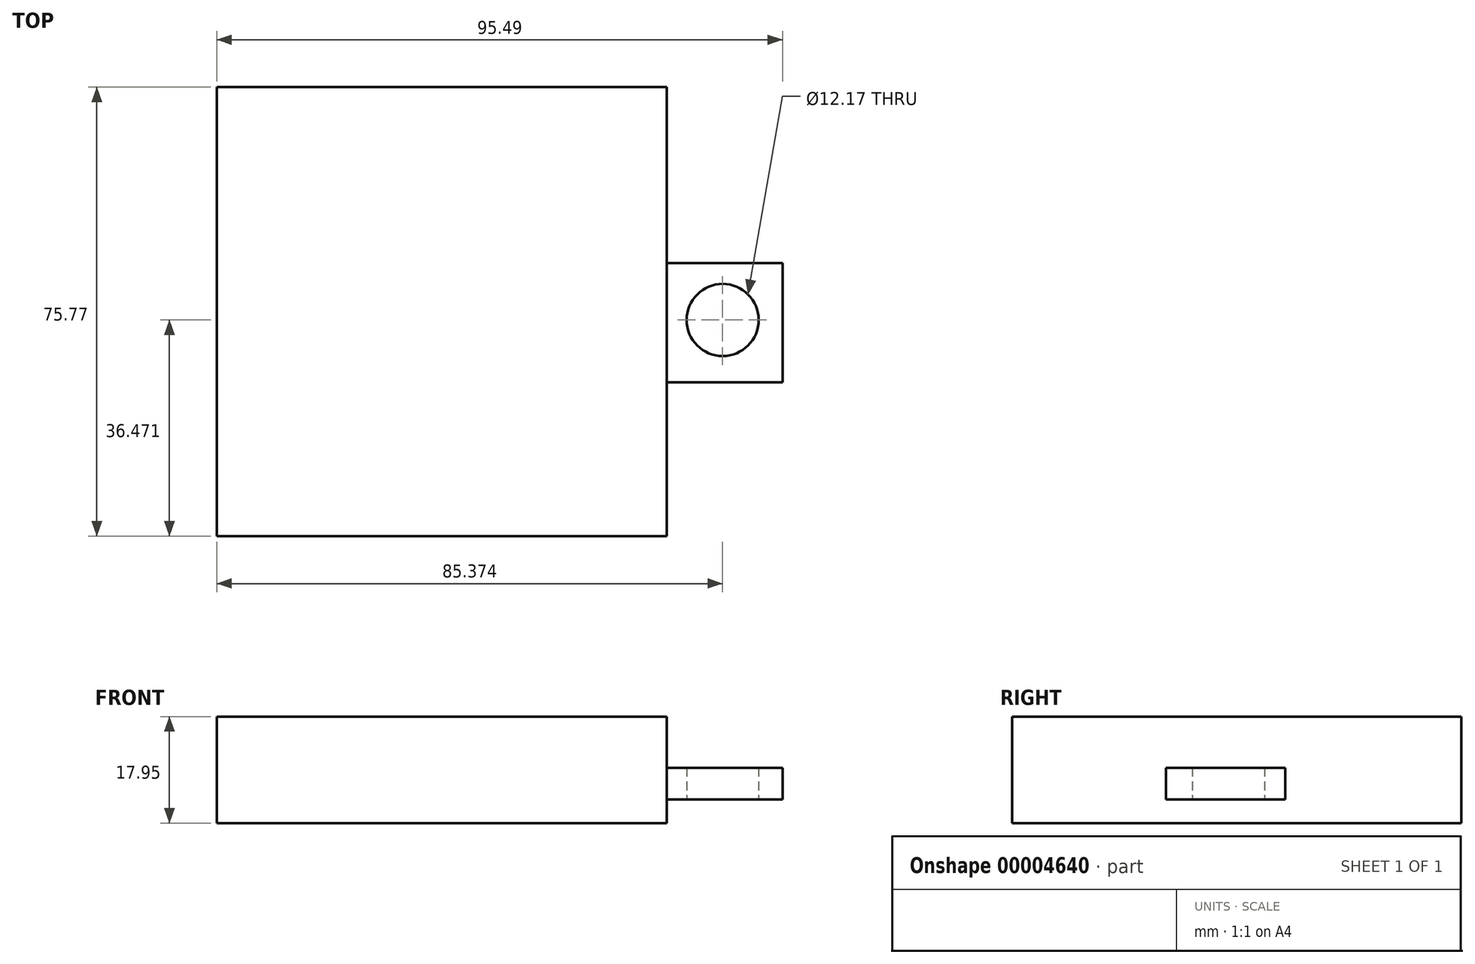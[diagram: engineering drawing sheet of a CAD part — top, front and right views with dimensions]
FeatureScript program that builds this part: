
annotation { "Feature Type Name" : "Feature", "Feature Type Description" : "" }
export const myFeature = defineFeature(function(context is Context, id is Id, definition is map)
    precondition{}
    {
        {
            var Q0;
            Q0=qCreatedBy(makeId("Top.planeOp"),FACE);
            var sketch = newSketch(context, id + "F0", { "sketchPlane" : qUnion([Q0])});
            skLineSegment(sketch, "E0.bottom", {"start": v(0, 75.77) * mm, "end": v(-75.95, 75.77) * mm});
            skLineSegment(sketch, "E0.top", {"start": v(0, 0) * mm, "end": v(-75.95, 0) * mm});
            skLineSegment(sketch, "E0.left", {"start": v(0, 75.77) * mm, "end": v(0, 0) * mm});
            skLineSegment(sketch, "E0.right", {"start": v(-75.95, 75.77) * mm, "end": v(-75.95, 0) * mm});
            skLineSegment(sketch, "E1", {"start": v(-37.98, 75.77) * mm, "end": v(-37.98, 0) * mm, "construction": true});
            skLineSegment(sketch, "E2", {"start": v(-75.95, 37.88) * mm, "end": v(0, 37.88) * mm, "construction": true});
            skSolve(sketch);
        }
        {
            var Q0;
            Q0=makeQuery(id+"F0.imprint","IMPRINT",FACE,{"disambiguationData":[TD([[makeQuery(id+"F0.imprint","IMPRINT",EDGE,{"derivedFrom":sQuery(id+"F0.wireOp",EDGE,"E0.bottom")}),1.0]])]});
            extrude(context, id + "F1", {"entities" : qUnion([Q0]), "depth" : 17.95 * mm});
        }
        {
            var Q0;
            Q0=makeQuery(id+"F1.opExtrude","CAP_FACE",FACE,{"disambiguationData":[OSD([sQuery(id+"F0.wireOp",EDGE,"E0.bottom"),sQuery(id+"F0.wireOp",EDGE,"E0.top"),sQuery(id+"F0.wireOp",EDGE,"E0.left"),sQuery(id+"F0.wireOp",EDGE,"E0.right")])],"isStart":false});
            var sketch = newSketch(context, id + "F2", { "sketchPlane" : qUnion([Q0])});
            skCircle(sketch, "E3", {"center": v(-56.36, 57.02) * mm, "radius": 10.58 * mm});
            skCircle(sketch, "E4", {"center": v(-57.1, 19.32) * mm, "radius": 11.67 * mm});
            skCircle(sketch, "E5", {"center": v(-20.17, 19.13) * mm, "radius": 11.7 * mm});
            skCircle(sketch, "E6", {"center": v(-20.36, 57.2) * mm, "radius": 12.12 * mm});
            skSolve(sketch);
        }
        {
            var Q0;
            Q0=makeQuery(id+"F1.opExtrude","SWEPT_FACE",FACE,{"disambiguationData":[OSD([sQuery(id+"F0.wireOp",EDGE,"E0.left")])]});
            var sketch = newSketch(context, id + "F3", { "sketchPlane" : qUnion([Q0])});
            skLineSegment(sketch, "E7.bottom", {"start": v(46.08, 9.33) * mm, "end": v(25.92, 9.33) * mm});
            skLineSegment(sketch, "E7.top", {"start": v(46.08, 4) * mm, "end": v(25.92, 4) * mm});
            skLineSegment(sketch, "E7.left", {"start": v(46.08, 9.33) * mm, "end": v(46.08, 4) * mm});
            skLineSegment(sketch, "E7.right", {"start": v(25.92, 9.33) * mm, "end": v(25.92, 4) * mm});
            skSolve(sketch);
        }
        {
            var Q0;
            Q0=makeQuery(id+"F3.imprint","IMPRINT",FACE,{"disambiguationData":[TD([[makeQuery(id+"F3.imprint","IMPRINT",EDGE,{"derivedFrom":sQuery(id+"F3.wireOp",EDGE,"E7.bottom")}),1.0]])]});
            extrude(context, id + "F4", {"entities" : qUnion([Q0]), "operationType" : NewBodyOperationType.ADD, "depth" : 19.54 * mm});
        }
        {
            var Q0;
            Q0=makeQuery(id+"F4.opExtrude","SWEPT_FACE",FACE,{"disambiguationData":[OSD([sQuery(id+"F3.wireOp",EDGE,"E7.top")])]});
            var sketch = newSketch(context, id + "F5", { "sketchPlane" : qUnion([Q0])});
            skCircle(sketch, "E8", {"center": v(9.42, -36.47) * mm, "radius": 6.08 * mm});
            skSolve(sketch);
        }
        {
            var Q0;
            Q0=makeQuery(id+"F5.imprint","IMPRINT",FACE,{"disambiguationData":[TD([[makeQuery(id+"F5.imprint","IMPRINT",EDGE,{"derivedFrom":sQuery(id+"F5.wireOp",EDGE,"E8")}),1.0]])]});
            extrude(context, id + "F6", {"entities" : qUnion([Q0]), "operationType" : NewBodyOperationType.REMOVE, "oppositeDirection" : true, "depth" : 25.4 * mm});
        }
    });
